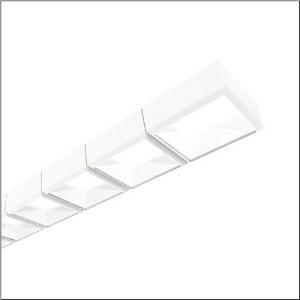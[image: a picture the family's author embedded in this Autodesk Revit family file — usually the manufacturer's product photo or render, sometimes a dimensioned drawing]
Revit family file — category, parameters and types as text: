
# Revit family: scriptus_r__11_5mz312d04wa_0fc2
name_source: partatom
category: Lighting Fixtures
units: mm (PartAtom-declared; Revit-internal decimal feet)

## family parameters
Cut with Voids When Loaded = No
Host = Face
Light Source = No
Part Type = Normal
Room Calculation Point = No
Round Connector Dimension = Use Diameter
Shared = No

## types (1)
- Scriptus® 11 (1 x LED 4000K / CRI = 80 (unbekannt), 1610 lm / 2410 lm, 4000K)
    Apparent Load = 62 VA
    CIE Flux Codes = - - - 0 100 / 82 95 99 100 100
    Color Rendering = 80
    Color Temperature = 4000K
    Default Elevation = 1800 mm
    Description = Scriptus® 11, office luminaire, primary optical cover: lenses, CAT 2 (L<= 3000cd/m²), light emission: direct/indirect distribution, primary light characteristic: symmetric, installation type: suspended mounting, LED, rated luminous flux: 8.020lm, luminous efficacy: 130lm/W, light colour: 840, colour temperature: 4000K, control gear: DALI, with terminal, 5-pole, mains connection: 230V, AC, 50Hz, rated input power: 62W, LED, control gear: ECG DALI, housing, luminaire housing, of aluminium, traffic white (RAL 9016), length: 1.658mm, width: 114mm, height: 57mm, protection rating (complete): IP20, insulation class (complete): insulation class I (protective earthing), certification: CE, ENEC, VDE, protection symbol: F, permissible operating ambient temperature: 0..+35°C, standard: EN 50419, packaging unit: 1 piece
    Height = 57 mm
    Lamp = 1 x LED 4000K / CRI >= 80 (unbekannt)
    Lamp Light Flux = 1610 lm / 2410 lm
    Lamp count = 1
    Length = 1658 mm
    Luminous efficacy = 131 lm/W
    Manufacturer = Siteco
    ModVariant = No
    Model = 5MZ312D04WA
    Mounting Place = Ceiling
    Mounting Type = Pendant
    Number of Poles = 1
    OnlyDefault = Yes
    Power Factor = 1
    Product Name = Scriptus® 11
    Product group = office luminaire | ceiling pendant
    ProductGroupID = 903
    Protection Class = Protection class I
    Protection Degree = IP 20
    RLX_Detail_Level = 1
    RLX_Emergency_Light_Flux = 0 lm
    RLX_Emergency_Type = 0
    RLX_Emergency_Type_DB = No
    RlxData = <blob elided: 31157 chars, md5=11822f43>
    Socket = socket
    Standby Power = 0 W
    System Light Flux = 8040 lm
    System Power = 62 W
    Type Comments = Product without accessories
    Type Image = l_1004839.jpg
    URL = http://relux.com
    VarID = ---
    Voltage = 0 V
    Weight = 0.00 kg
    Width = 114 mm

## geometry (parser evidence)
native form markers: Blend x4, Sweep x19
no freeform markers — native parametric forms only
